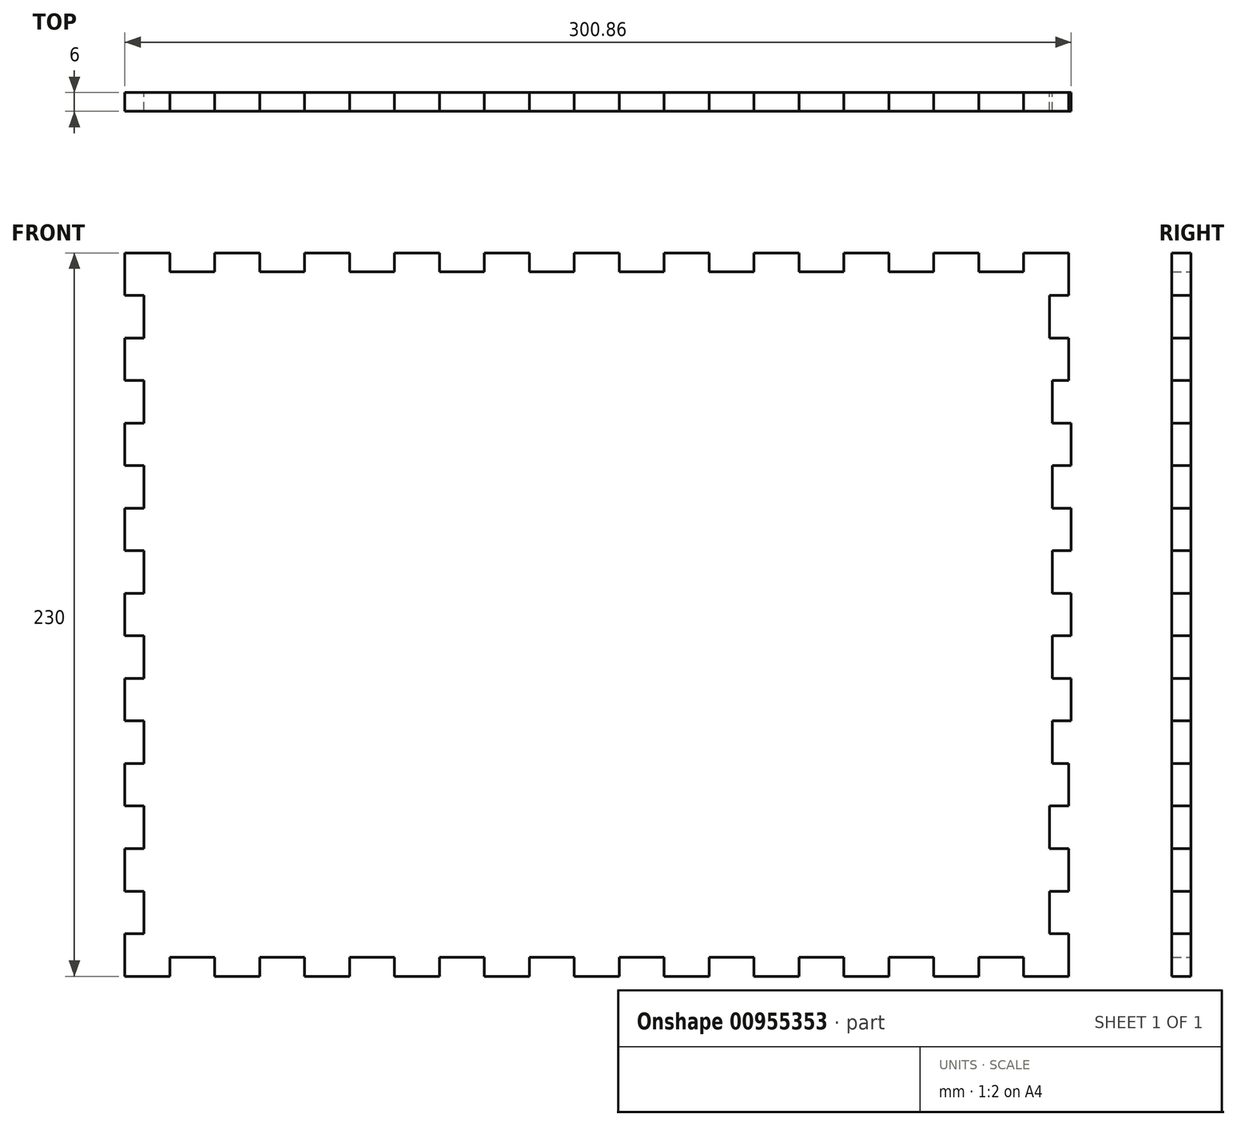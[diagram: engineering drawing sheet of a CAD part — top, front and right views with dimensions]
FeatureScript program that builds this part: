
annotation { "Feature Type Name" : "Feature", "Feature Type Description" : "" }
export const myFeature = defineFeature(function(context is Context, id is Id, definition is map)
    precondition{}
    {
        {
            var Q0;
            Q0=qCreatedBy(makeId("Front.planeOp"),FACE);
            var sketch = newSketch(context, id + "F0", { "sketchPlane" : qUnion([Q0])});
            skLineSegment(sketch, "E0.left", {"start": v(149.57, 115) * mm, "end": v(149.57, 115.47) * mm});
            skLineSegment(sketch, "E1", {"start": v(-150.43, 115) * mm, "end": v(-136.14, 115) * mm});
            skLineSegment(sketch, "E2", {"start": v(-136.14, 115) * mm, "end": v(-136.14, 109) * mm});
            skLineSegment(sketch, "E3", {"start": v(-136.14, 109) * mm, "end": v(-121.86, 109) * mm});
            skLineSegment(sketch, "E4", {"start": v(-121.86, 109) * mm, "end": v(-121.86, 115) * mm});
            skLineSegment(sketch, "E5", {"start": v(-121.86, 115) * mm, "end": v(-107.57, 115) * mm});
            skLineSegment(sketch, "E6.1.0.1", {"start": v(-93.29, 115) * mm, "end": v(-79, 115) * mm});
            skLineSegment(sketch, "E6.1.0.2", {"start": v(-107.57, 109) * mm, "end": v(-93.29, 109) * mm});
            skLineSegment(sketch, "E6.1.0.3", {"start": v(-107.57, 115) * mm, "end": v(-107.57, 109) * mm});
            skLineSegment(sketch, "E6.1.0.4", {"start": v(-93.29, 109) * mm, "end": v(-93.29, 115) * mm});
            skLineSegment(sketch, "E6.2.0.0", {"start": v(-93.29, 115) * mm, "end": v(-79, 115) * mm});
            skLineSegment(sketch, "E6.2.0.1", {"start": v(-64.72, 115) * mm, "end": v(-50.43, 115) * mm});
            skLineSegment(sketch, "E6.2.0.2", {"start": v(-79, 109) * mm, "end": v(-64.72, 109) * mm});
            skLineSegment(sketch, "E6.2.0.3", {"start": v(-79, 115) * mm, "end": v(-79, 109) * mm});
            skLineSegment(sketch, "E6.2.0.4", {"start": v(-64.72, 109) * mm, "end": v(-64.72, 115) * mm});
            skLineSegment(sketch, "E6.3.0.0", {"start": v(-64.72, 115) * mm, "end": v(-50.43, 115) * mm});
            skLineSegment(sketch, "E6.3.0.1", {"start": v(-36.14, 115) * mm, "end": v(-21.86, 115) * mm});
            skLineSegment(sketch, "E6.3.0.2", {"start": v(-50.43, 109) * mm, "end": v(-36.14, 109) * mm});
            skLineSegment(sketch, "E6.3.0.3", {"start": v(-50.43, 115) * mm, "end": v(-50.43, 109) * mm});
            skLineSegment(sketch, "E6.3.0.4", {"start": v(-36.14, 109) * mm, "end": v(-36.14, 115) * mm});
            skLineSegment(sketch, "E6.4.0.0", {"start": v(-36.14, 115) * mm, "end": v(-21.86, 115) * mm});
            skLineSegment(sketch, "E6.4.0.1", {"start": v(-7.57, 115) * mm, "end": v(6.71, 115) * mm});
            skLineSegment(sketch, "E6.4.0.2", {"start": v(-21.86, 109) * mm, "end": v(-7.57, 109) * mm});
            skLineSegment(sketch, "E6.4.0.3", {"start": v(-21.86, 115) * mm, "end": v(-21.86, 109) * mm});
            skLineSegment(sketch, "E6.4.0.4", {"start": v(-7.57, 109) * mm, "end": v(-7.57, 115) * mm});
            skLineSegment(sketch, "E6.5.0.0", {"start": v(-7.57, 115) * mm, "end": v(6.71, 115) * mm});
            skLineSegment(sketch, "E6.5.0.1", {"start": v(21, 115) * mm, "end": v(35.28, 115) * mm});
            skLineSegment(sketch, "E6.5.0.2", {"start": v(6.71, 109) * mm, "end": v(21, 109) * mm});
            skLineSegment(sketch, "E6.5.0.3", {"start": v(6.71, 115) * mm, "end": v(6.71, 109) * mm});
            skLineSegment(sketch, "E6.5.0.4", {"start": v(21, 109) * mm, "end": v(21, 115) * mm});
            skLineSegment(sketch, "E6.6.0.0", {"start": v(21, 115) * mm, "end": v(35.28, 115) * mm});
            skLineSegment(sketch, "E6.6.0.1", {"start": v(49.57, 115) * mm, "end": v(63.86, 115) * mm});
            skLineSegment(sketch, "E6.6.0.2", {"start": v(35.28, 109) * mm, "end": v(49.57, 109) * mm});
            skLineSegment(sketch, "E6.6.0.3", {"start": v(35.28, 115) * mm, "end": v(35.28, 109) * mm});
            skLineSegment(sketch, "E6.6.0.4", {"start": v(49.57, 109) * mm, "end": v(49.57, 115) * mm});
            skLineSegment(sketch, "E6.7.0.0", {"start": v(49.57, 115) * mm, "end": v(63.86, 115) * mm});
            skLineSegment(sketch, "E6.7.0.1", {"start": v(78.14, 115) * mm, "end": v(92.43, 115) * mm});
            skLineSegment(sketch, "E6.7.0.2", {"start": v(63.86, 109) * mm, "end": v(78.14, 109) * mm});
            skLineSegment(sketch, "E6.7.0.3", {"start": v(63.86, 115) * mm, "end": v(63.86, 109) * mm});
            skLineSegment(sketch, "E6.7.0.4", {"start": v(78.14, 109) * mm, "end": v(78.14, 115) * mm});
            skLineSegment(sketch, "E6.8.0.0", {"start": v(78.14, 115) * mm, "end": v(92.43, 115) * mm});
            skLineSegment(sketch, "E6.8.0.1", {"start": v(106.71, 115) * mm, "end": v(121, 115) * mm});
            skLineSegment(sketch, "E6.8.0.2", {"start": v(92.43, 109) * mm, "end": v(106.71, 109) * mm});
            skLineSegment(sketch, "E6.8.0.3", {"start": v(92.43, 115) * mm, "end": v(92.43, 109) * mm});
            skLineSegment(sketch, "E6.8.0.4", {"start": v(106.71, 109) * mm, "end": v(106.71, 115) * mm});
            skLineSegment(sketch, "E6.9.0.0", {"start": v(106.71, 115) * mm, "end": v(121, 115) * mm});
            skLineSegment(sketch, "E6.9.0.1", {"start": v(135.28, 115) * mm, "end": v(149.57, 115) * mm});
            skLineSegment(sketch, "E6.9.0.2", {"start": v(121, 109) * mm, "end": v(135.28, 109) * mm});
            skLineSegment(sketch, "E6.9.0.3", {"start": v(121, 115) * mm, "end": v(121, 109) * mm});
            skLineSegment(sketch, "E6.9.0.4", {"start": v(135.28, 109) * mm, "end": v(135.28, 115) * mm});
            skLineSegment(sketch, "E6.direction1", {"start": v(-150.43, 115) * mm, "end": v(-121.86, 115) * mm, "construction": true});
            skLineSegment(sketch, "E7.MirrorCS", {"start": v(-121.86, -109) * mm, "end": v(-121.86, -115) * mm});
            skLineSegment(sketch, "E8.MirrorCS", {"start": v(-93.29, -109) * mm, "end": v(-93.29, -115) * mm});
            skLineSegment(sketch, "E9.MirrorCS", {"start": v(-107.57, -115) * mm, "end": v(-107.57, -109) * mm});
            skLineSegment(sketch, "E10.MirrorCS", {"start": v(92.43, -115) * mm, "end": v(92.43, -109) * mm});
            skLineSegment(sketch, "E11.MirrorCS", {"start": v(-64.72, -109) * mm, "end": v(-64.72, -115) * mm});
            skLineSegment(sketch, "E12.MirrorCS", {"start": v(6.71, -115) * mm, "end": v(6.71, -109) * mm});
            skLineSegment(sketch, "E13.MirrorCS", {"start": v(121, -115) * mm, "end": v(121, -109) * mm});
            skLineSegment(sketch, "E14.MirrorCS", {"start": v(-79, -115) * mm, "end": v(-79, -109) * mm});
            skLineSegment(sketch, "E15.MirrorCS", {"start": v(-7.57, -109) * mm, "end": v(-7.57, -115) * mm});
            skLineSegment(sketch, "E16.MirrorCS", {"start": v(21, -109) * mm, "end": v(21, -115) * mm});
            skLineSegment(sketch, "E17.MirrorCS", {"start": v(-50.43, -115) * mm, "end": v(-50.43, -109) * mm});
            skLineSegment(sketch, "E18.MirrorCS", {"start": v(-36.14, -109) * mm, "end": v(-36.14, -115) * mm});
            skLineSegment(sketch, "E19.MirrorCS", {"start": v(78.14, -109) * mm, "end": v(78.14, -115) * mm});
            skLineSegment(sketch, "E20.MirrorCS", {"start": v(-21.86, -115) * mm, "end": v(-21.86, -109) * mm});
            skLineSegment(sketch, "E21.MirrorCS", {"start": v(35.28, -115) * mm, "end": v(35.28, -109) * mm});
            skLineSegment(sketch, "E22.MirrorCS", {"start": v(106.71, -109) * mm, "end": v(106.71, -115) * mm});
            skLineSegment(sketch, "E23.MirrorCS", {"start": v(49.57, -109) * mm, "end": v(49.57, -115) * mm});
            skLineSegment(sketch, "E24.MirrorCS", {"start": v(63.86, -115) * mm, "end": v(63.86, -109) * mm});
            skLineSegment(sketch, "E25.MirrorCS", {"start": v(-136.14, -115) * mm, "end": v(-136.14, -109) * mm});
            skLineSegment(sketch, "E26.MirrorCS", {"start": v(135.28, -109) * mm, "end": v(135.28, -115) * mm});
            skLineSegment(sketch, "E27.MirrorCS", {"start": v(49.57, -115) * mm, "end": v(63.86, -115) * mm});
            skLineSegment(sketch, "E28.MirrorCS", {"start": v(-93.29, -115) * mm, "end": v(-79, -115) * mm});
            skLineSegment(sketch, "E29.MirrorCS", {"start": v(-36.14, -115) * mm, "end": v(-21.86, -115) * mm});
            skLineSegment(sketch, "E30.MirrorCS", {"start": v(21, -115) * mm, "end": v(35.28, -115) * mm});
            skLineSegment(sketch, "E31.MirrorCS", {"start": v(78.14, -115) * mm, "end": v(92.43, -115) * mm});
            skLineSegment(sketch, "E32.MirrorCS", {"start": v(106.71, -115) * mm, "end": v(121, -115) * mm});
            skLineSegment(sketch, "E33.MirrorCS", {"start": v(-150.43, -115) * mm, "end": v(-136.14, -115) * mm});
            skLineSegment(sketch, "E34.MirrorCS", {"start": v(-7.57, -115) * mm, "end": v(6.71, -115) * mm});
            skLineSegment(sketch, "E35.MirrorCS", {"start": v(-121.86, -115) * mm, "end": v(-107.57, -115) * mm});
            skLineSegment(sketch, "E36.MirrorCS", {"start": v(-64.72, -115) * mm, "end": v(-50.43, -115) * mm});
            skLineSegment(sketch, "E37.MirrorCS", {"start": v(135.28, -115) * mm, "end": v(149.57, -115) * mm});
            skLineSegment(sketch, "E38.MirrorCS", {"start": v(63.86, -109) * mm, "end": v(78.14, -109) * mm});
            skLineSegment(sketch, "E39.MirrorCS", {"start": v(-21.86, -109) * mm, "end": v(-7.57, -109) * mm});
            skLineSegment(sketch, "E40.MirrorCS", {"start": v(-150.43, -115) * mm, "end": v(-121.86, -115) * mm, "construction": true});
            skLineSegment(sketch, "E41.MirrorCS", {"start": v(35.28, -109) * mm, "end": v(49.57, -109) * mm});
            skLineSegment(sketch, "E42.MirrorCS", {"start": v(6.71, -109) * mm, "end": v(21, -109) * mm});
            skLineSegment(sketch, "E43.MirrorCS", {"start": v(-107.57, -109) * mm, "end": v(-93.29, -109) * mm});
            skLineSegment(sketch, "E44.MirrorCS", {"start": v(92.43, -109) * mm, "end": v(106.71, -109) * mm});
            skLineSegment(sketch, "E45.MirrorCS", {"start": v(121, -109) * mm, "end": v(135.28, -109) * mm});
            skLineSegment(sketch, "E46.MirrorCS", {"start": v(-136.14, -109) * mm, "end": v(-121.86, -109) * mm});
            skLineSegment(sketch, "E47.MirrorCS", {"start": v(-79, -109) * mm, "end": v(-64.72, -109) * mm});
            skLineSegment(sketch, "E48.MirrorCS", {"start": v(-50.43, -109) * mm, "end": v(-36.14, -109) * mm});
            skLineSegment(sketch, "E49", {"start": v(-150.43, -115) * mm, "end": v(-150.43, -101.47) * mm});
            skLineSegment(sketch, "E50", {"start": v(-150.43, -101.47) * mm, "end": v(-144.43, -101.47) * mm});
            skLineSegment(sketch, "E51", {"start": v(-144.43, -101.47) * mm, "end": v(-144.43, -87.94) * mm});
            skLineSegment(sketch, "E52", {"start": v(-144.43, -87.94) * mm, "end": v(-150.43, -87.94) * mm});
            skLineSegment(sketch, "E53", {"start": v(-150.43, -87.94) * mm, "end": v(-150.43, -74.41) * mm});
            skLineSegment(sketch, "E54.1.0.0", {"start": v(-144.43, -60.88) * mm, "end": v(-150.43, -60.88) * mm});
            skLineSegment(sketch, "E54.1.0.2", {"start": v(-144.43, -74.41) * mm, "end": v(-144.43, -60.88) * mm});
            skLineSegment(sketch, "E54.1.0.3", {"start": v(-150.43, -60.88) * mm, "end": v(-150.43, -47.35) * mm});
            skLineSegment(sketch, "E54.1.0.4", {"start": v(-150.43, -74.41) * mm, "end": v(-144.43, -74.41) * mm});
            skLineSegment(sketch, "E54.2.0.0", {"start": v(-144.43, -33.82) * mm, "end": v(-150.43, -33.82) * mm});
            skLineSegment(sketch, "E54.2.0.1", {"start": v(-150.43, -60.88) * mm, "end": v(-150.43, -47.35) * mm});
            skLineSegment(sketch, "E54.2.0.2", {"start": v(-144.43, -47.35) * mm, "end": v(-144.43, -33.82) * mm});
            skLineSegment(sketch, "E54.2.0.3", {"start": v(-150.43, -33.82) * mm, "end": v(-150.43, -20.3) * mm});
            skLineSegment(sketch, "E54.2.0.4", {"start": v(-150.43, -47.35) * mm, "end": v(-144.43, -47.35) * mm});
            skLineSegment(sketch, "E54.direction1", {"start": v(-150.43, -115) * mm, "end": v(-150.43, -87.94) * mm, "construction": true});
            skLineSegment(sketch, "E55.0.3.0", {"start": v(-144.43, -6.76) * mm, "end": v(-150.43, -6.76) * mm});
            skLineSegment(sketch, "E55.6.3.0", {"start": v(-144.43, -20.3) * mm, "end": v(-144.43, -6.76) * mm});
            skLineSegment(sketch, "E55.9.3.0", {"start": v(-150.43, -6.76) * mm, "end": v(-150.43, 6.76) * mm});
            skLineSegment(sketch, "E55.12.3.0", {"start": v(-150.43, -20.3) * mm, "end": v(-144.43, -20.3) * mm});
            skLineSegment(sketch, "E55.0.4.0", {"start": v(-144.43, 20.3) * mm, "end": v(-150.43, 20.3) * mm});
            skLineSegment(sketch, "E55.3.4.0", {"start": v(-150.43, -6.76) * mm, "end": v(-150.43, 6.76) * mm});
            skLineSegment(sketch, "E55.6.4.0", {"start": v(-144.43, 6.76) * mm, "end": v(-144.43, 20.3) * mm});
            skLineSegment(sketch, "E55.9.4.0", {"start": v(-150.43, 20.3) * mm, "end": v(-150.43, 33.82) * mm});
            skLineSegment(sketch, "E55.12.4.0", {"start": v(-150.43, 6.76) * mm, "end": v(-144.43, 6.76) * mm});
            skLineSegment(sketch, "E56.0.5.0", {"start": v(-144.43, 47.35) * mm, "end": v(-150.43, 47.35) * mm});
            skLineSegment(sketch, "E56.6.5.0", {"start": v(-144.43, 33.82) * mm, "end": v(-144.43, 47.35) * mm});
            skLineSegment(sketch, "E56.9.5.0", {"start": v(-150.43, 47.35) * mm, "end": v(-150.43, 60.88) * mm});
            skLineSegment(sketch, "E56.12.5.0", {"start": v(-150.43, 33.82) * mm, "end": v(-144.43, 33.82) * mm});
            skLineSegment(sketch, "E56.0.6.0", {"start": v(-144.43, 74.41) * mm, "end": v(-150.43, 74.41) * mm});
            skLineSegment(sketch, "E56.3.6.0", {"start": v(-150.43, 47.35) * mm, "end": v(-150.43, 60.88) * mm});
            skLineSegment(sketch, "E56.6.6.0", {"start": v(-144.43, 60.88) * mm, "end": v(-144.43, 74.41) * mm});
            skLineSegment(sketch, "E56.9.6.0", {"start": v(-150.43, 74.41) * mm, "end": v(-150.43, 87.94) * mm});
            skLineSegment(sketch, "E56.12.6.0", {"start": v(-150.43, 60.88) * mm, "end": v(-144.43, 60.88) * mm});
            skLineSegment(sketch, "E57.0.7.0", {"start": v(-144.43, 101.47) * mm, "end": v(-150.43, 101.47) * mm});
            skLineSegment(sketch, "E57.6.7.0", {"start": v(-144.43, 87.94) * mm, "end": v(-144.43, 101.47) * mm});
            skLineSegment(sketch, "E57.9.7.0", {"start": v(-150.43, 101.47) * mm, "end": v(-150.43, 115) * mm});
            skLineSegment(sketch, "E57.12.7.0", {"start": v(-150.43, 87.94) * mm, "end": v(-144.43, 87.94) * mm});
            skLineSegment(sketch, "E58.MirrorCS", {"start": v(150.43, -33.82) * mm, "end": v(150.43, -20.3) * mm});
            skLineSegment(sketch, "E59.MirrorCS", {"start": v(150.43, 6.76) * mm, "end": v(144.43, 6.76) * mm});
            skLineSegment(sketch, "E60.MirrorCS", {"start": v(150.43, 33.82) * mm, "end": v(144.43, 33.82) * mm});
            skLineSegment(sketch, "E61.MirrorCS", {"start": v(150.43, 60.88) * mm, "end": v(144.43, 60.88) * mm});
            skLineSegment(sketch, "E62.MirrorCS", {"start": v(144.43, 20.3) * mm, "end": v(150.43, 20.3) * mm});
            skLineSegment(sketch, "E63.MirrorCS", {"start": v(149.57, -60.88) * mm, "end": v(149.57, -47.35) * mm});
            skLineSegment(sketch, "E64.MirrorCS", {"start": v(144.43, -6.76) * mm, "end": v(150.43, -6.76) * mm});
            skLineSegment(sketch, "E65.MirrorCS", {"start": v(144.43, 60.88) * mm, "end": v(144.43, 74.41) * mm});
            skLineSegment(sketch, "E66.MirrorCS", {"start": v(144.43, 6.76) * mm, "end": v(144.43, 20.3) * mm});
            skLineSegment(sketch, "E67.MirrorCS", {"start": v(150.43, -20.3) * mm, "end": v(144.43, -20.3) * mm});
            skLineSegment(sketch, "E68.MirrorCS", {"start": v(144.43, 74.41) * mm, "end": v(149.57, 74.41) * mm});
            skLineSegment(sketch, "E69.MirrorCS", {"start": v(149.57, -47.35) * mm, "end": v(144.43, -47.35) * mm});
            skLineSegment(sketch, "E70.MirrorCS", {"start": v(144.43, -33.82) * mm, "end": v(150.43, -33.82) * mm});
            skLineSegment(sketch, "E71.MirrorCS", {"start": v(143.57, -101.47) * mm, "end": v(143.57, -87.94) * mm});
            skLineSegment(sketch, "E72.MirrorCS", {"start": v(143.57, -87.94) * mm, "end": v(149.57, -87.94) * mm});
            skLineSegment(sketch, "E73.MirrorCS", {"start": v(143.57, -60.88) * mm, "end": v(149.57, -60.88) * mm});
            skLineSegment(sketch, "E74.MirrorCS", {"start": v(149.57, -74.41) * mm, "end": v(143.57, -74.41) * mm});
            skLineSegment(sketch, "E75.MirrorCS", {"start": v(149.57, 101.47) * mm, "end": v(149.57, 115) * mm});
            skLineSegment(sketch, "E76.MirrorCS", {"start": v(143.57, 101.47) * mm, "end": v(149.57, 101.47) * mm});
            skLineSegment(sketch, "E77.MirrorCS", {"start": v(144.43, 33.82) * mm, "end": v(144.43, 47.35) * mm});
            skLineSegment(sketch, "E78.MirrorCS", {"start": v(144.43, 47.35) * mm, "end": v(150.43, 47.35) * mm});
            skLineSegment(sketch, "E79.MirrorCS", {"start": v(149.57, -101.47) * mm, "end": v(143.57, -101.47) * mm});
            skLineSegment(sketch, "E80.MirrorCS", {"start": v(149.57, 87.94) * mm, "end": v(143.57, 87.94) * mm});
            skLineSegment(sketch, "E81.MirrorCS", {"start": v(150.43, 47.35) * mm, "end": v(150.43, 60.88) * mm});
            skLineSegment(sketch, "E82.MirrorCS", {"start": v(150.43, -6.76) * mm, "end": v(150.43, 6.76) * mm});
            skLineSegment(sketch, "E83.MirrorCS", {"start": v(150.43, 20.3) * mm, "end": v(150.43, 33.82) * mm});
            skLineSegment(sketch, "E84.MirrorCS", {"start": v(149.57, -87.94) * mm, "end": v(149.57, -74.41) * mm});
            skLineSegment(sketch, "E85.MirrorCS", {"start": v(149.57, -115) * mm, "end": v(149.57, -101.47) * mm});
            skLineSegment(sketch, "E86.MirrorCS", {"start": v(149.57, -115) * mm, "end": v(149.57, -87.94) * mm, "construction": true});
            skLineSegment(sketch, "E87.MirrorCS", {"start": v(143.57, -74.41) * mm, "end": v(143.57, -60.88) * mm});
            skLineSegment(sketch, "E88.MirrorCS", {"start": v(144.43, -47.35) * mm, "end": v(144.43, -33.82) * mm});
            skLineSegment(sketch, "E89.MirrorCS", {"start": v(144.43, -20.3) * mm, "end": v(144.43, -6.76) * mm});
            skLineSegment(sketch, "E90.MirrorCS", {"start": v(149.57, 74.41) * mm, "end": v(149.57, 87.94) * mm});
            skLineSegment(sketch, "E91.MirrorCS", {"start": v(143.57, 87.94) * mm, "end": v(143.57, 101.47) * mm});
            skSolve(sketch);
        }
        {
            var Q0;
            Q0=makeQuery(id+"F0.imprint","IMPRINT",FACE,{"disambiguationData":[TD([[makeQuery(id+"F0.imprint","IMPRINT",EDGE,{"derivedFrom":sQuery(id+"F0.wireOp",EDGE,"E1")}),-1.0]])]});
            extrude(context, id + "F1", {"entities" : qUnion([Q0]), "depth" : 6 * mm, "offsetDistance" : 25 * mm});
        }
    });
